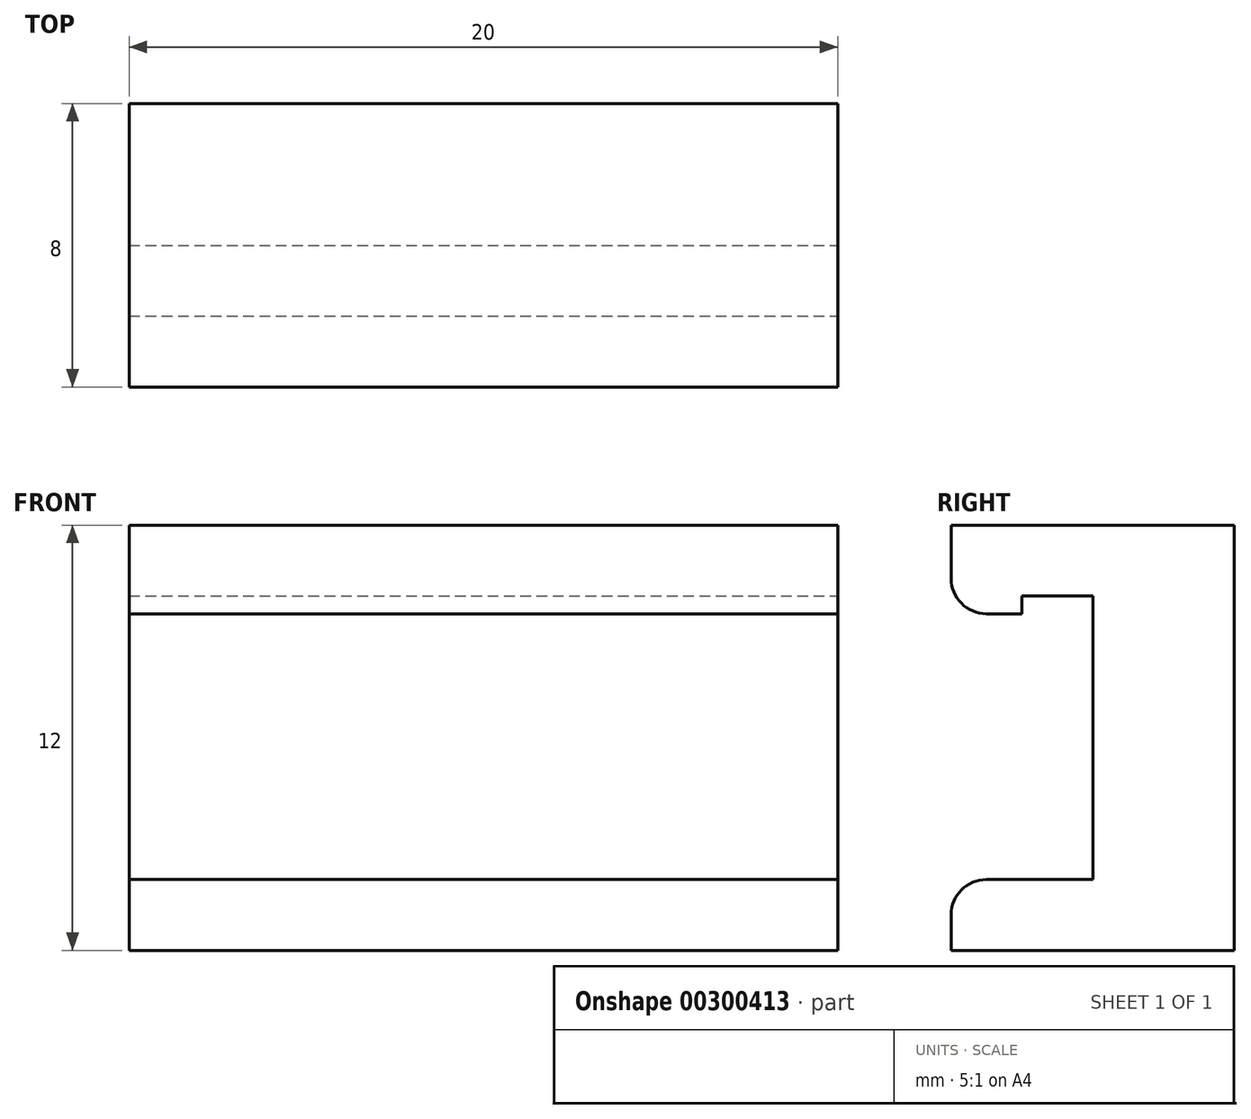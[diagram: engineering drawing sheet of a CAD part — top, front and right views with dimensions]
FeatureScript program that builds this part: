
annotation { "Feature Type Name" : "Feature", "Feature Type Description" : "" }
export const myFeature = defineFeature(function(context is Context, id is Id, definition is map)
    precondition{}
    {
        {
            var Q0;
            Q0=qCreatedBy(makeId("Front.planeOp"),FACE);
            var sketch = newSketch(context, id + "F0", { "sketchPlane" : qUnion([Q0])});
            skLineSegment(sketch, "E0.right", {"start": v(-5, 4) * mm, "end": v(-5, -4) * mm});
            skPoint(sketch, "E0.middle", {"position": v(0, 0) * mm});
            skLineSegment(sketch, "E1", {"start": v(-5, 4) * mm, "end": v(15, 4) * mm});
            skLineSegment(sketch, "E2", {"start": v(-5, -4) * mm, "end": v(15, -4) * mm});
            skLineSegment(sketch, "E3", {"start": v(-5, 4) * mm, "end": v(-5, 6) * mm});
            skLineSegment(sketch, "E4", {"start": v(-5, 6) * mm, "end": v(15, 6) * mm});
            skLineSegment(sketch, "E5", {"start": v(15, 6) * mm, "end": v(15, 4) * mm});
            skLineSegment(sketch, "E6", {"start": v(-5, -4) * mm, "end": v(-5, -6) * mm});
            skLineSegment(sketch, "E7", {"start": v(-5, -6) * mm, "end": v(15, -6) * mm});
            skLineSegment(sketch, "E8", {"start": v(15, -6) * mm, "end": v(15, -4) * mm});
            skLineSegment(sketch, "E9", {"start": v(15, 4) * mm, "end": v(15, -4) * mm});
            skSolve(sketch);
        }
        {
            var Q0;
            Q0=makeQuery(id+"F0.imprint","IMPRINT",FACE,{"disambiguationData":[TD([[makeQuery(id+"F0.imprint","IMPRINT",EDGE,{"derivedFrom":sQuery(id+"F0.wireOp",EDGE,"E0.right")}),1.0]])]});
            extrude(context, id + "F1", {"entities" : qUnion([Q0]), "depth" : 4 * mm});
        }
        {
            var Q0;
            Q0=makeQuery(id+"F0.imprint","IMPRINT",FACE,{"disambiguationData":[TD([[makeQuery(id+"F0.imprint","IMPRINT",EDGE,{"derivedFrom":sQuery(id+"F0.wireOp",EDGE,"E1")}),1.0]])]});
            var Q1;
            Q1=makeQuery(id+"F0.imprint","IMPRINT",FACE,{"disambiguationData":[TD([[makeQuery(id+"F0.imprint","IMPRINT",EDGE,{"derivedFrom":sQuery(id+"F0.wireOp",EDGE,"E2")}),-1.0]])]});
            extrude(context, id + "F2", {"entities" : qUnion([Q0, Q1]), "operationType" : NewBodyOperationType.ADD, "depth" : 8 * mm});
        }
        {
            var Q0;
            Q0=makeQuery(id+"F2.opExtrude","SWEPT_FACE",FACE,{"disambiguationData":[OSD([sQuery(id+"F0.wireOp",EDGE,"E1")])]});
            var sketch = newSketch(context, id + "F3", { "sketchPlane" : qUnion([Q0])});
            skLineSegment(sketch, "E10", {"start": v(-5, 8) * mm, "end": v(-5, 6) * mm});
            skLineSegment(sketch, "E11", {"start": v(-5, 6) * mm, "end": v(15, 6) * mm});
            skLineSegment(sketch, "E12", {"start": v(15, 6) * mm, "end": v(15, 8) * mm});
            skSolve(sketch);
        }
        {
            var Q0;
            Q0=makeQuery(id+"F3.imprint","IMPRINT",FACE,{"disambiguationData":[TD([[makeQuery(id+"F3.imprint","IMPRINT",EDGE,{"derivedFrom":sQuery(id+"F3.wireOp",EDGE,"E10")}),1.0]])]});
            extrude(context, id + "F4", {"entities" : qUnion([Q0]), "operationType" : NewBodyOperationType.ADD, "depth" : 0.5 * mm});
        }
        {
            var Q0;
            Q0=makeQuery(id+"F4.opExtrude","CAP_EDGE",EDGE,{"disambiguationData":[OSD([sQuery(id+"F0.wireOp",EDGE,"E1")])],"isStart":false});
            var Q1;
            Q1=makeQuery(id+"F2.opExtrude","CAP_EDGE",EDGE,{"disambiguationData":[OSD([sQuery(id+"F0.wireOp",EDGE,"E2")])],"isStart":false});
            fillet(context, id + "F5", {"entities" : qUnion([Q0, Q1]), "radius" : 1 * mm, "tangentPropagation" : true, "allowEdgeOverflow" : false});
        }
    });
